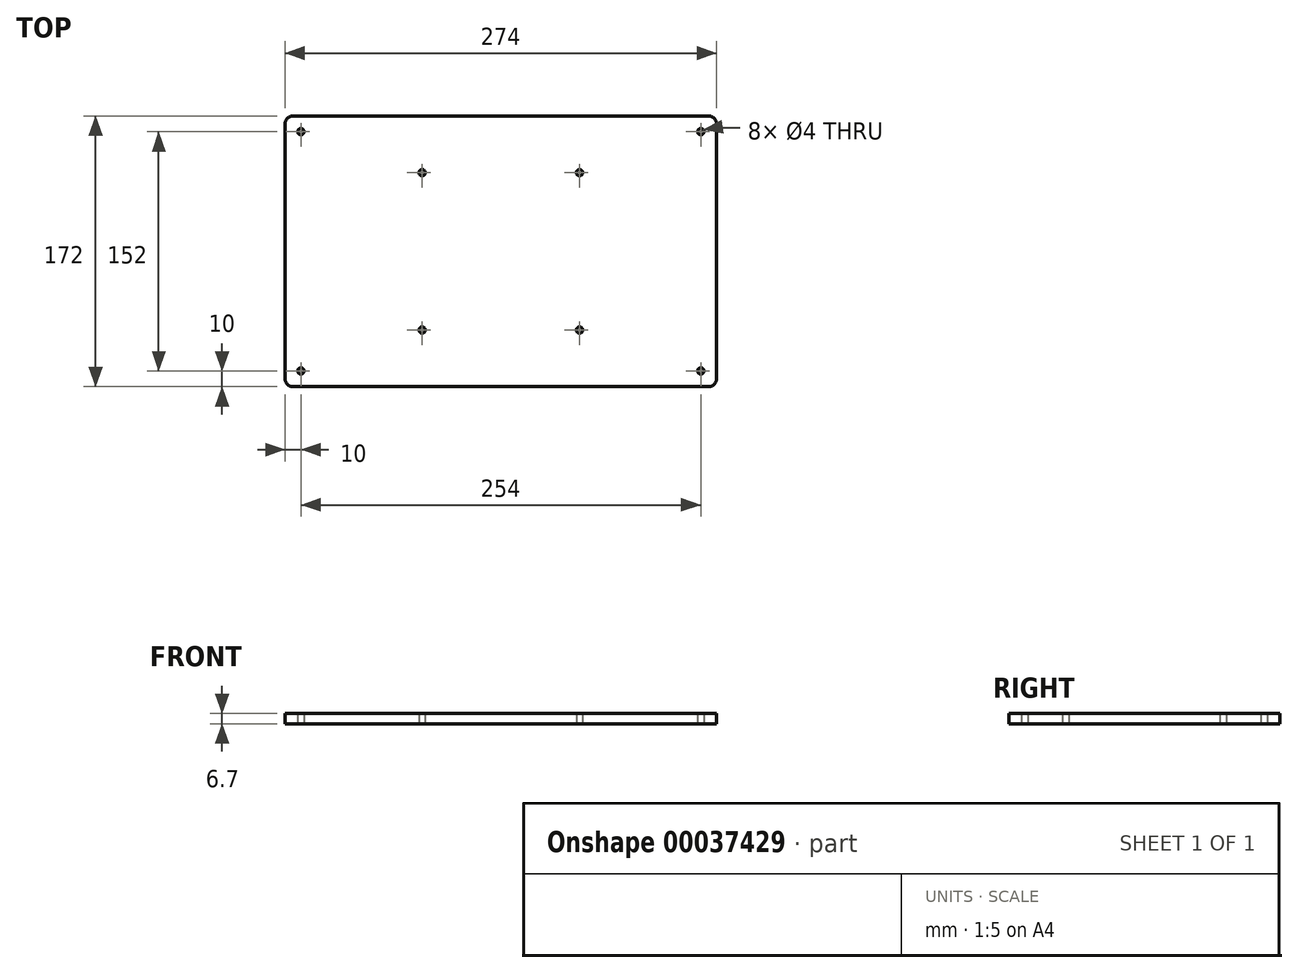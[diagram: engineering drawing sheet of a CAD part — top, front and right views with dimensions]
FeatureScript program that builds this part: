
annotation { "Feature Type Name" : "Feature", "Feature Type Description" : "" }
export const myFeature = defineFeature(function(context is Context, id is Id, definition is map)
    precondition{}
    {
        {
            var Q0;
            Q0=qCreatedBy(makeId("Top.planeOp"),FACE);
            var sketch = newSketch(context, id + "F0", { "sketchPlane" : qUnion([Q0])});
            skLineSegment(sketch, "E0.rect.bottom", {"start": v(50, 50) * mm, "end": v(-50, 50) * mm, "construction": true});
            skLineSegment(sketch, "E0.rect.top", {"start": v(50, -50) * mm, "end": v(-50, -50) * mm, "construction": true});
            skLineSegment(sketch, "E0.rect.left", {"start": v(50, 50) * mm, "end": v(50, -50) * mm, "construction": true});
            skLineSegment(sketch, "E0.rect.right", {"start": v(-50, 50) * mm, "end": v(-50, -50) * mm, "construction": true});
            skPoint(sketch, "E0.rect.middle", {"position": v(0, 0) * mm});
            skLineSegment(sketch, "E1.rect.bottom", {"start": v(127, 76) * mm, "end": v(-127, 76) * mm, "construction": true});
            skLineSegment(sketch, "E1.rect.top", {"start": v(127, -76) * mm, "end": v(-127, -76) * mm, "construction": true});
            skLineSegment(sketch, "E1.rect.left", {"start": v(127, 76) * mm, "end": v(127, -76) * mm, "construction": true});
            skLineSegment(sketch, "E1.rect.right", {"start": v(-127, 76) * mm, "end": v(-127, -76) * mm, "construction": true});
            skLineSegment(sketch, "E2.rect.bottom", {"start": v(132, 86) * mm, "end": v(-132, 86) * mm});
            skLineSegment(sketch, "E2.rect.top", {"start": v(132, -86) * mm, "end": v(-132, -86) * mm});
            skLineSegment(sketch, "E2.rect.left", {"start": v(137, 81) * mm, "end": v(137, -81) * mm});
            skLineSegment(sketch, "E2.rect.right", {"start": v(-137, 81) * mm, "end": v(-137, -81) * mm});
            skCircle(sketch, "E3", {"center": v(-127, 76) * mm, "radius": 2 * mm});
            skCircle(sketch, "E4", {"center": v(-50, 50) * mm, "radius": 2 * mm});
            skCircle(sketch, "E5", {"center": v(50, 50) * mm, "radius": 2 * mm});
            skCircle(sketch, "E6", {"center": v(50, -50) * mm, "radius": 2 * mm});
            skCircle(sketch, "E7", {"center": v(-50, -50) * mm, "radius": 2 * mm});
            skCircle(sketch, "E8", {"center": v(-127, -76) * mm, "radius": 2 * mm});
            skCircle(sketch, "E9", {"center": v(127, -76) * mm, "radius": 2 * mm});
            skCircle(sketch, "E10", {"center": v(127, 76) * mm, "radius": 2 * mm});
            skPoint(sketch, "E11.visualSharp", {"position": v(-137, 86) * mm});
            skArc(sketch, "E11.filletArc", {"start": v(-132, 86) * mm, "mid": v(-135.54, 84.54) * mm, "end": v(-137, 81) * mm});
            skPoint(sketch, "E12.visualSharp", {"position": v(137, -86) * mm});
            skArc(sketch, "E12.filletArc", {"start": v(132, -86) * mm, "mid": v(135.54, -84.54) * mm, "end": v(137, -81) * mm});
            skPoint(sketch, "E13.visualSharp", {"position": v(-137, -86) * mm});
            skArc(sketch, "E13.filletArc", {"start": v(-137, -81) * mm, "mid": v(-135.54, -84.54) * mm, "end": v(-132, -86) * mm});
            skPoint(sketch, "E14.visualSharp", {"position": v(137, 86) * mm});
            skArc(sketch, "E14.filletArc", {"start": v(137, 81) * mm, "mid": v(135.54, 84.54) * mm, "end": v(132, 86) * mm});
            skSolve(sketch);
        }
        {
            var Q0;
            Q0 = qSketchRegion(id + "F0", true);
            extrude(context, id + "F1", {"entities" : qUnion([Q0]), "depth" : 6.7 * mm});
        }
    });
